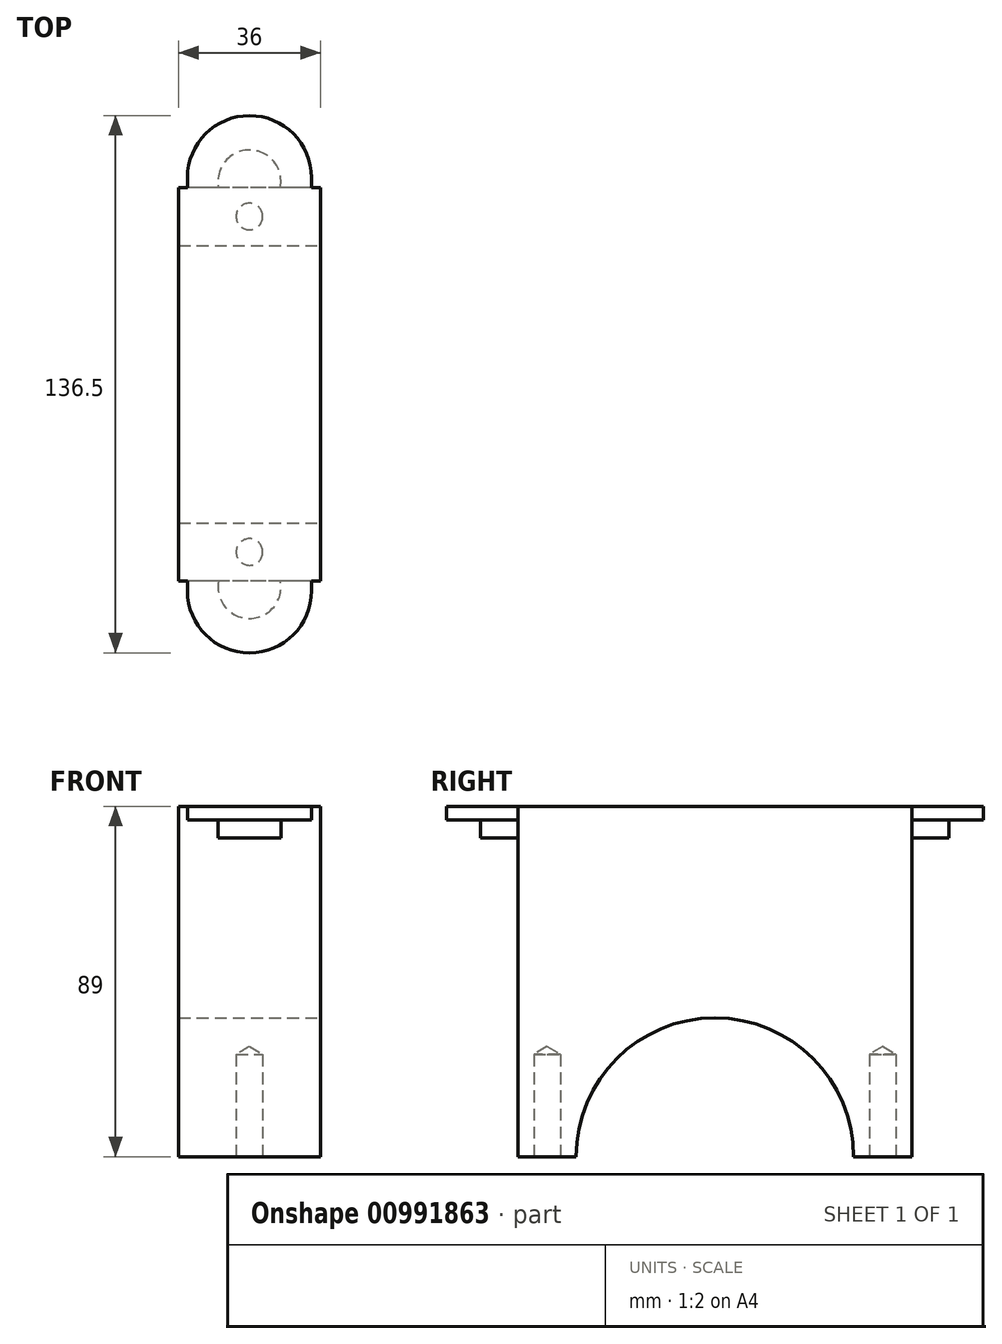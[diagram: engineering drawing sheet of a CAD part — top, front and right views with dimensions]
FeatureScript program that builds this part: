
annotation { "Feature Type Name" : "Feature", "Feature Type Description" : "" }
export const myFeature = defineFeature(function(context is Context, id is Id, definition is map)
    precondition{}
    {
        {
            var Q0;
            Q0=qCreatedBy(makeId("Top.planeOp"),FACE);
            var sketch = newSketch(context, id + "F0", { "sketchPlane" : qUnion([Q0])});
            skLineSegment(sketch, "E0.bottom", {"start": v(18, -50) * mm, "end": v(-18, -50) * mm});
            skLineSegment(sketch, "E0.top", {"start": v(18, 50) * mm, "end": v(-18, 50) * mm});
            skLineSegment(sketch, "E0.left", {"start": v(18, -50) * mm, "end": v(18, 50) * mm});
            skLineSegment(sketch, "E0.right", {"start": v(-18, -50) * mm, "end": v(-18, 50) * mm});
            skPoint(sketch, "E0.middle", {"position": v(0, 0) * mm});
            skSolve(sketch);
        }
        {
            var Q0;
            Q0 = qSketchRegion(id + "F0", true);
            extrude(context, id + "F1", {"entities" : qUnion([Q0]), "depth" : 89 * mm, "offsetDistance" : 25 * mm});
        }
        {
            var Q0;
            Q0=qCreatedBy(makeId("Front.planeOp"),FACE);
            var sketch = newSketch(context, id + "F2", { "sketchPlane" : qUnion([Q0])});
            skCircle(sketch, "E1", {"center": v(0, 0) * mm, "radius": 10.25 * mm});
            skSolve(sketch);
        }
        {
            var Q0;
            Q0 = qSketchRegion(id + "F2", true);
            extrude(context, id + "F3", {"entities" : qUnion([Q0]), "operationType" : NewBodyOperationType.REMOVE, "oppositeDirection" : true, "depth" : 50 * mm, "offsetDistance" : 25 * mm, "symmetric" : true});
        }
        {
            var Q0;
            Q0=qCreatedBy(makeId("Right.planeOp"),FACE);
            var sketch = newSketch(context, id + "F4", { "sketchPlane" : qUnion([Q0])});
            skCircle(sketch, "E2", {"center": v(0, 0) * mm, "radius": 35.25 * mm});
            skSolve(sketch);
        }
        {
            var Q0;
            Q0 = qSketchRegion(id + "F4", true);
            extrude(context, id + "F5", {"entities" : qUnion([Q0]), "operationType" : NewBodyOperationType.REMOVE, "oppositeDirection" : true, "depth" : 55 * mm, "offsetDistance" : 25 * mm, "symmetric" : true});
        }
        {
            var Q0;
            Q0=makeQuery(id+"F1.opExtrude","CAP_FACE",FACE,{"disambiguationData":[OSD([sQuery(id+"F0.wireOp",EDGE,"E0.bottom"),sQuery(id+"F0.wireOp",EDGE,"E0.top"),sQuery(id+"F0.wireOp",EDGE,"E0.left"),sQuery(id+"F0.wireOp",EDGE,"E0.right")])],"isStart":false});
            var sketch = newSketch(context, id + "F6", { "sketchPlane" : qUnion([Q0])});
            skCircle(sketch, "E3", {"center": v(0, 52.5) * mm, "radius": 15.75 * mm});
            skCircle(sketch, "E4", {"center": v(0, -52.5) * mm, "radius": 15.75 * mm});
            skSolve(sketch);
        }
        {
            var Q0;
            Q0 = qSketchRegion(id + "F6", true);
            extrude(context, id + "F7", {"entities" : qUnion([Q0]), "operationType" : NewBodyOperationType.ADD, "oppositeDirection" : true, "depth" : 3.5 * mm, "offsetDistance" : 25 * mm});
        }
        {
            var Q0;
            Q0=makeQuery(id+"F7.boolean.opBoolean","MERGE",FACE,{"derivedFrom":[makeQuery(id+"F1.opExtrude","CAP_FACE",FACE,{"disambiguationData":[OSD([sQuery(id+"F0.wireOp",EDGE,"E0.bottom"),sQuery(id+"F0.wireOp",EDGE,"E0.top"),sQuery(id+"F0.wireOp",EDGE,"E0.left"),sQuery(id+"F0.wireOp",EDGE,"E0.right")])],"isStart":false}),makeQuery(id+"F7.opExtrude","CAP_FACE",FACE,{"disambiguationData":[OSD([sQuery(id+"F6.wireOp",EDGE,"E3")])],"isStart":true}),makeQuery(id+"F7.opExtrude","CAP_FACE",FACE,{"disambiguationData":[OSD([sQuery(id+"F6.wireOp",EDGE,"E4")])],"isStart":true})]});
            var sketch = newSketch(context, id + "F8", { "sketchPlane" : qUnion([Q0])});
            skLineSegment(sketch, "E5.bottom", {"start": v(15.75, -52.5) * mm, "end": v(-15.75, -52.5) * mm});
            skLineSegment(sketch, "E5.top", {"start": v(15.75, 52.5) * mm, "end": v(-15.75, 52.5) * mm});
            skLineSegment(sketch, "E5.left", {"start": v(15.75, -52.5) * mm, "end": v(15.75, 52.5) * mm});
            skLineSegment(sketch, "E5.right", {"start": v(-15.75, -52.5) * mm, "end": v(-15.75, 52.5) * mm});
            skPoint(sketch, "E5.middle", {"position": v(0, 0) * mm});
            skSolve(sketch);
        }
        {
            var Q0;
            Q0 = qSketchRegion(id + "F8", true);
            extrude(context, id + "F9", {"entities" : qUnion([Q0]), "operationType" : NewBodyOperationType.ADD, "oppositeDirection" : true, "depth" : 3.5 * mm, "offsetDistance" : 25 * mm});
        }
        {
            var Q0;
            Q0=makeQuery(id+"F9.boolean.opBoolean","MERGE",FACE,{"derivedFrom":[makeQuery(id+"F7.boolean.opBoolean","MERGE",FACE,{"derivedFrom":[makeQuery(id+"F1.opExtrude","CAP_FACE",FACE,{"disambiguationData":[OSD([sQuery(id+"F0.wireOp",EDGE,"E0.bottom"),sQuery(id+"F0.wireOp",EDGE,"E0.top"),sQuery(id+"F0.wireOp",EDGE,"E0.left"),sQuery(id+"F0.wireOp",EDGE,"E0.right")])],"isStart":false}),makeQuery(id+"F7.opExtrude","CAP_FACE",FACE,{"disambiguationData":[OSD([sQuery(id+"F6.wireOp",EDGE,"E3")])],"isStart":true}),makeQuery(id+"F7.opExtrude","CAP_FACE",FACE,{"disambiguationData":[OSD([sQuery(id+"F6.wireOp",EDGE,"E4")])],"isStart":true})]}),makeQuery(id+"F9.opExtrude","CAP_FACE",FACE,{"disambiguationData":[OSD([sQuery(id+"F8.wireOp",EDGE,"E5.bottom"),sQuery(id+"F8.wireOp",EDGE,"E5.top"),sQuery(id+"F8.wireOp",EDGE,"E5.left"),sQuery(id+"F8.wireOp",EDGE,"E5.right")])],"isStart":true})]});
            var sketch = newSketch(context, id + "F10", { "sketchPlane" : qUnion([Q0])});
            skCircle(sketch, "E6", {"center": v(0, 51.5) * mm, "radius": 8 * mm});
            skCircle(sketch, "E7", {"center": v(0, -51.5) * mm, "radius": 8 * mm});
            skSolve(sketch);
        }
        {
            var Q0;
            Q0 = qSketchRegion(id + "F10", true);
            extrude(context, id + "F11", {"entities" : qUnion([Q0]), "operationType" : NewBodyOperationType.ADD, "oppositeDirection" : true, "depth" : 8 * mm, "offsetDistance" : 25 * mm});
        }
        {
            var Q0;
            {var subQ0=sQuery(id+"F0.wireOp",EDGE,"E0.bottom");var subQ1=sQuery(id+"F0.wireOp",EDGE,"E0.right");var subQ2=sQuery(id+"F0.wireOp",EDGE,"E0.left");Q0=makeQuery(id+"F5.boolean.opBoolean","SPLIT",FACE,{"disambiguationData":[TD([makeQuery(id+"F1.opExtrude","SWEPT_FACE",FACE,{"disambiguationData":[OSD([subQ0])]})])],"derivedFrom":makeQuery(id+"F1.opExtrude","CAP_FACE",FACE,{"disambiguationData":[OSD([subQ0,sQuery(id+"F0.wireOp",EDGE,"E0.top"),subQ2,subQ1])],"isStart":true})});}
            var sketch = newSketch(context, id + "F12", { "sketchPlane" : qUnion([Q0])});
            skPoint(sketch, "E8", {"position": v(0, 42.62) * mm});
            skPoint(sketch, "E8.positionSnap0", {"position": v(18, 42.62) * mm});
            skSolve(sketch);
        }
        {
            var Q0;
            Q0=sQuery(id+"F12.wireOp",VERTEX,"E8");
            var Q1;
            Q1=makeQuery(id+"F1.opExtrude","SWEPT_BODY",BODY,{"disambiguationData":[OSD([sQuery(id+"F0.wireOp",EDGE,"E0.bottom"),sQuery(id+"F0.wireOp",EDGE,"E0.top"),sQuery(id+"F0.wireOp",EDGE,"E0.left"),sQuery(id+"F0.wireOp",EDGE,"E0.right")])]});
            hole(context, id + "F13", {"style" : HoleStyle.SIMPLE, "endStyle" : HoleEndStyle.BLIND, "standardTappedOrClearance" : lookupTablePath({ "fit" : "Free", "standard" : "ANSI", "size" : "1/4", "type" : "Clearance" }), "standardBlindInLast" : lookupTablePath({ "fit" : "Free", "standard" : "ANSI", "engagement" : "75%", "pitch" : "20 tpi", "size" : "1/4", "type" : "Clearance & tapped" }), "holeDiameter" : 6.76 * mm, "majorDiameter" : 5 * mm, "holeDepth" : 26 * mm, "isTappedThrough" : true, "tappedDepth" : 12 * mm, "tapClearance" : 3, "locations" : qUnion([Q0]), "scope" : qUnion([Q1])});
        }
        {
            var Q0;
            {var subQ0=sQuery(id+"F0.wireOp",EDGE,"E0.top");var subQ1=sQuery(id+"F0.wireOp",EDGE,"E0.left");var subQ2=sQuery(id+"F0.wireOp",EDGE,"E0.right");Q0=makeQuery(id+"F5.boolean.opBoolean","SPLIT",FACE,{"disambiguationData":[TD([makeQuery(id+"F1.opExtrude","SWEPT_FACE",FACE,{"disambiguationData":[OSD([subQ0])]})])],"derivedFrom":makeQuery(id+"F1.opExtrude","CAP_FACE",FACE,{"disambiguationData":[OSD([sQuery(id+"F0.wireOp",EDGE,"E0.bottom"),subQ0,subQ1,subQ2])],"isStart":true})});}
            var sketch = newSketch(context, id + "F14", { "sketchPlane" : qUnion([Q0])});
            skPoint(sketch, "E9", {"position": v(0, -42.62) * mm});
            skSolve(sketch);
        }
        {
            var Q0;
            Q0=sQuery(id+"F14.wireOp",VERTEX,"E9");
            var Q1;
            Q1=makeQuery(id+"F1.opExtrude","SWEPT_BODY",BODY,{"disambiguationData":[OSD([sQuery(id+"F0.wireOp",EDGE,"E0.bottom"),sQuery(id+"F0.wireOp",EDGE,"E0.top"),sQuery(id+"F0.wireOp",EDGE,"E0.left"),sQuery(id+"F0.wireOp",EDGE,"E0.right")])]});
            hole(context, id + "F15", {"style" : HoleStyle.SIMPLE, "endStyle" : HoleEndStyle.BLIND, "standardTappedOrClearance" : lookupTablePath({ "fit" : "Free", "standard" : "ANSI", "size" : "1/4", "type" : "Clearance" }), "standardBlindInLast" : lookupTablePath({ "fit" : "Free", "standard" : "ANSI", "engagement" : "75%", "pitch" : "20 tpi", "size" : "1/4", "type" : "Clearance & tapped" }), "holeDiameter" : 6.76 * mm, "majorDiameter" : 5 * mm, "holeDepth" : 26 * mm, "isTappedThrough" : true, "tappedDepth" : 12 * mm, "tapClearance" : 3, "locations" : qUnion([Q0]), "scope" : qUnion([Q1])});
        }
    });
